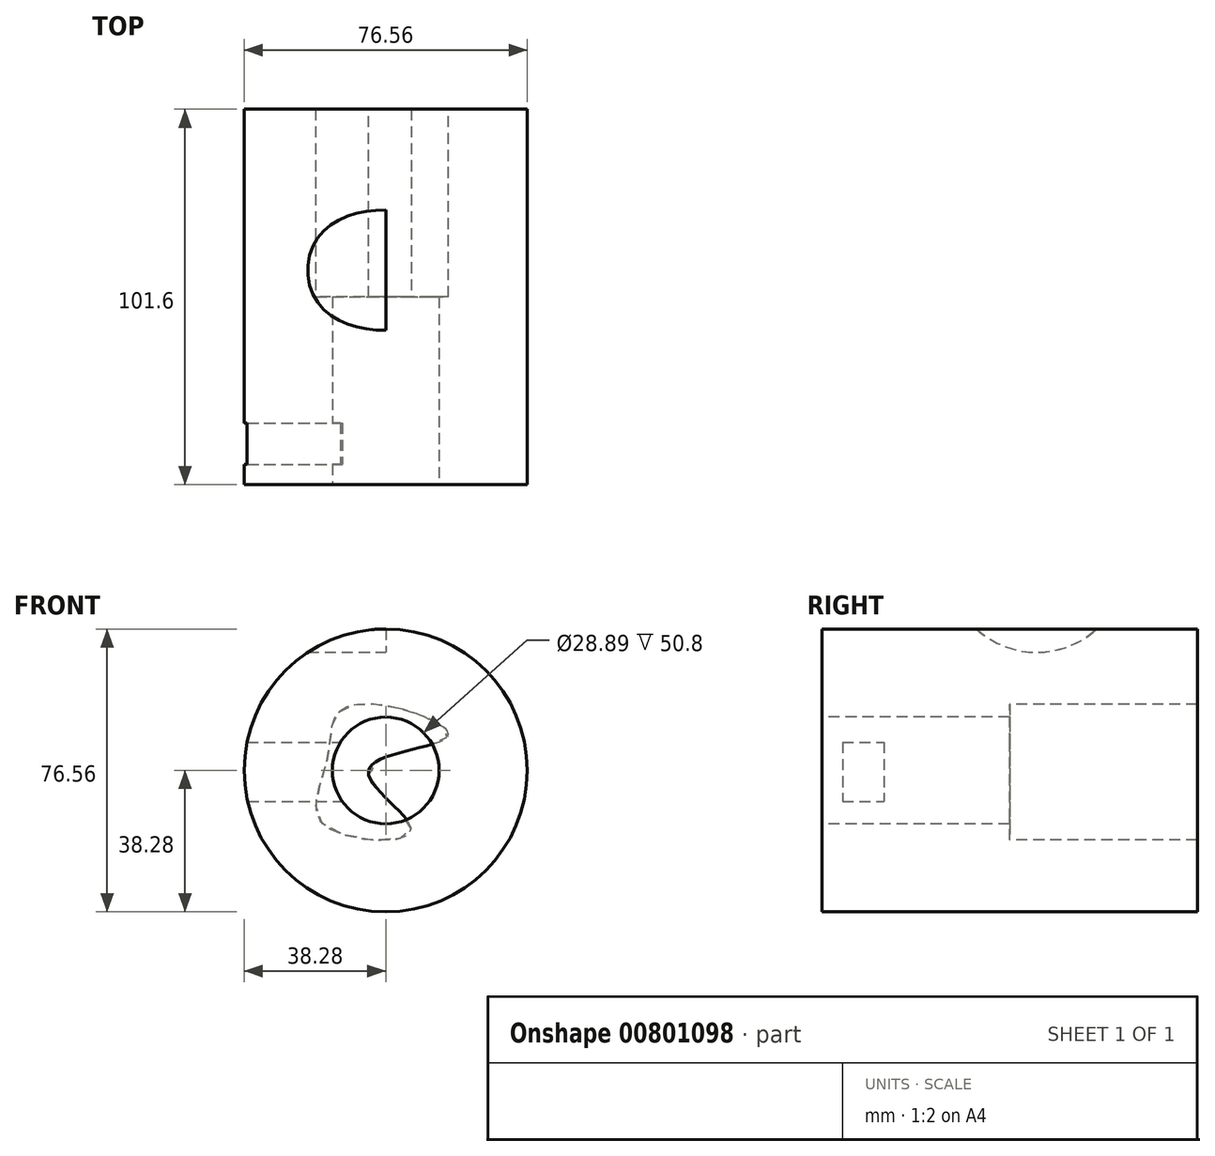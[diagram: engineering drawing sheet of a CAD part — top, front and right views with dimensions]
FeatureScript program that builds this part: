
annotation { "Feature Type Name" : "Feature", "Feature Type Description" : "" }
export const myFeature = defineFeature(function(context is Context, id is Id, definition is map)
    precondition{}
    {
        {
            var Q0;
            Q0=qCreatedBy(makeId("Front.planeOp"),FACE);
            var sketch = newSketch(context, id + "F0", { "sketchPlane" : qUnion([Q0])});
            skCircle(sketch, "E0", {"center": v(0, 0) * mm, "radius": 38.28 * mm});
            skSolve(sketch);
        }
        {
            var Q0;
            Q0 = qSketchRegion(id + "F0", true);
            extrude(context, id + "F1", {"entities" : qUnion([Q0]), "depth" : 101.6 * mm, "offsetDistance" : 25.4 * mm});
        }
        {
            var Q0;
            Q0=makeQuery(id+"F1.opExtrude","CAP_FACE",FACE,{"disambiguationData":[OSD([sQuery(id+"F0.wireOp",EDGE,"E0")])],"isStart":false});
            var sketch = newSketch(context, id + "F2", { "sketchPlane" : qUnion([Q0])});
            skCircle(sketch, "E1", {"center": v(0, 0) * mm, "radius": 14.44 * mm});
            skSolve(sketch);
        }
        {
            var Q0;
            Q0 = qSketchRegion(id + "F2", true);
            extrude(context, id + "F3", {"entities" : qUnion([Q0]), "operationType" : NewBodyOperationType.REMOVE, "oppositeDirection" : true, "depth" : 50.8 * mm, "offsetDistance" : 25.4 * mm});
        }
        {
            var Q0;
            Q0=qCreatedBy(makeId("Right.planeOp"),FACE);
            var sketch = newSketch(context, id + "F4", { "sketchPlane" : qUnion([Q0])});
            skLineSegment(sketch, "E2.bottom", {"start": v(-96.03, 7.68) * mm, "end": v(-84.84, 7.68) * mm});
            skLineSegment(sketch, "E2.top", {"start": v(-96.03, -8.44) * mm, "end": v(-84.84, -8.44) * mm});
            skLineSegment(sketch, "E2.left", {"start": v(-96.03, 7.68) * mm, "end": v(-96.03, -8.44) * mm});
            skLineSegment(sketch, "E2.right", {"start": v(-84.84, 7.68) * mm, "end": v(-84.84, -8.44) * mm});
            skSolve(sketch);
        }
        {
            var Q0;
            Q0=makeQuery(id+"F4.imprint","IMPRINT",FACE,{"disambiguationData":[TD([[makeQuery(id+"F4.imprint","IMPRINT",EDGE,{"derivedFrom":sQuery(id+"F4.wireOp",EDGE,"E2.bottom")}),-1.0]])]});
            extrude(context, id + "F5", {"entities" : qUnion([Q0]), "operationType" : NewBodyOperationType.REMOVE, "oppositeDirection" : true, "depth" : 76.2 * mm, "offsetDistance" : 25.4 * mm});
        }
        {
            var Q0;
            Q0=makeQuery(id+"F1.opExtrude","CAP_FACE",FACE,{"disambiguationData":[OSD([sQuery(id+"F0.wireOp",EDGE,"E0")])],"isStart":true});
            var sketch = newSketch(context, id + "F6", { "sketchPlane" : qUnion([Q0])});
            skFitSpline(sketch, "E3", {"points": [v(-3.5, 16.78) * mm, v(12.99, 15.45) * mm, v(16.02, 2.37) * mm, v(16.78, -14.7) * mm, v(-6.92, -16.21) * mm, v(4.65, 0) * mm, v(-16.59, 9) * mm, v(-3.5, 16.78) * mm]});
            skSolve(sketch);
        }
        {
            var Q0;
            Q0=makeQuery(id+"F6.imprint","IMPRINT",FACE,{"disambiguationData":[TD([[makeQuery(id+"F6.imprint","IMPRINT",EDGE,{"derivedFrom":sQuery(id+"F6.wireOp",EDGE,"E3")}),-1.0]])]});
            extrude(context, id + "F7", {"entities" : qUnion([Q0]), "operationType" : NewBodyOperationType.REMOVE, "oppositeDirection" : true, "depth" : 50.8 * mm, "offsetDistance" : 25.4 * mm});
        }
        {
            var Q0;
            Q0=qCreatedBy(makeId("Right.planeOp"),FACE);
            var sketch = newSketch(context, id + "F8", { "sketchPlane" : qUnion([Q0])});
            skCircle(sketch, "E4", {"center": v(-43.5, 56.03) * mm, "radius": 24.09 * mm});
            skSolve(sketch);
        }
        {
            var Q0;
            Q0=makeQuery(id+"F8.imprint","IMPRINT",FACE,{"disambiguationData":[TD([[makeQuery(id+"F8.imprint","IMPRINT",EDGE,{"derivedFrom":sQuery(id+"F8.wireOp",EDGE,"E4")}),1.0]])]});
            extrude(context, id + "F9", {"entities" : qUnion([Q0]), "operationType" : NewBodyOperationType.REMOVE, "oppositeDirection" : true, "depth" : 101.6 * mm, "offsetDistance" : 25.4 * mm});
        }
    });
